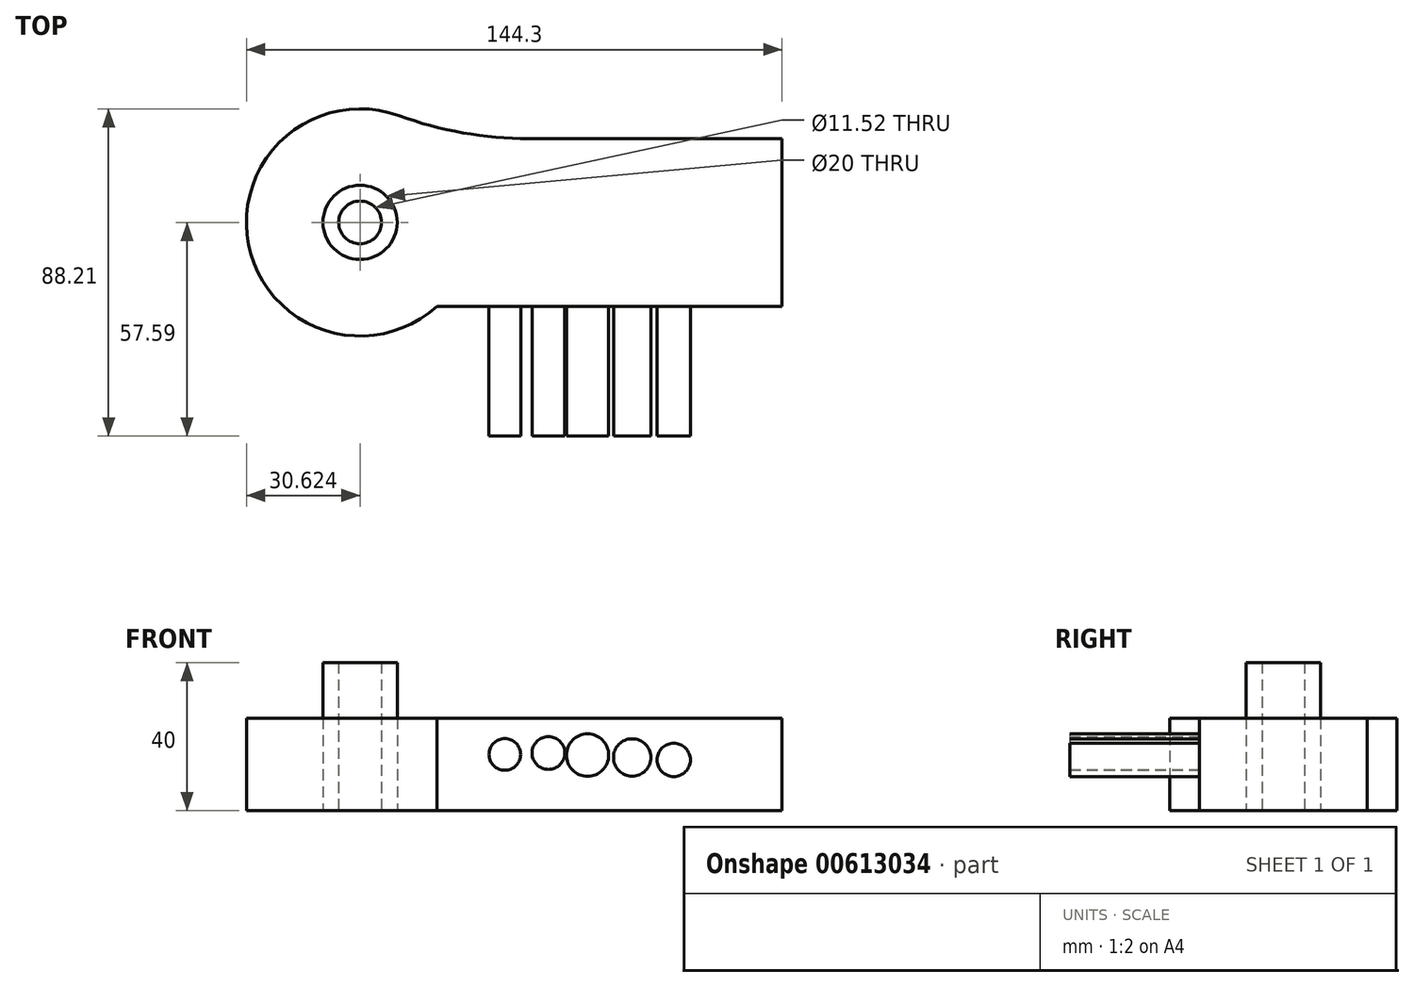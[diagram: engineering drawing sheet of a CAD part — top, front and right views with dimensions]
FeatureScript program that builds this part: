
annotation { "Feature Type Name" : "Feature", "Feature Type Description" : "" }
export const myFeature = defineFeature(function(context is Context, id is Id, definition is map)
    precondition{}
    {
        {
            var Q0;
            Q0=qCreatedBy(makeId("Top.planeOp"),FACE);
            var sketch = newSketch(context, id + "F0", { "sketchPlane" : qUnion([Q0])});
            skLineSegment(sketch, "E0.bottom", {"start": v(-54.54, 21.04) * mm, "end": v(59.14, 21.04) * mm});
            skLineSegment(sketch, "E0.top", {"start": v(-54.54, -24.14) * mm, "end": v(59.14, -24.14) * mm});
            skLineSegment(sketch, "E0.left", {"start": v(-54.54, 21.04) * mm, "end": v(-54.54, -24.14) * mm});
            skLineSegment(sketch, "E0.right", {"start": v(59.14, 21.04) * mm, "end": v(59.14, -24.14) * mm});
            skCircle(sketch, "E1", {"center": v(-54.54, -1.55) * mm, "radius": 30.62 * mm});
            skArc(sketch, "E2", {"start": v(-44.06, 27.22) * mm, "mid": v(-26.82, 22.6) * mm, "end": v(-9.04, 21.04) * mm});
            skCircle(sketch, "E3", {"center": v(-54.54, -1.55) * mm, "radius": 10 * mm});
            skCircle(sketch, "E4", {"center": v(-54.54, -1.55) * mm, "radius": 5.76 * mm});
            skSolve(sketch);
        }
        {
            var Q0;
            Q0 = qSketchRegion(id + "F0", true);
            extrude(context, id + "F1", {"entities" : qUnion([Q0]), "depth" : 25 * mm, "offsetDistance" : 25 * mm});
        }
        {
            var Q0;
            {var subQ0=sQuery(id+"F0.wireOp",EDGE,"E3");var subQ1=sQuery(id+"F0.wireOp",EDGE,"E0.left");var subQ2=makeQuery(id+"F0.imprint","INTERSECT",VERTEX,{"disambiguationData":[OD(0.0)],"derivedFrom":[subQ1,subQ0]});Q0=makeQuery(id+"F0.imprint","IMPRINT",FACE,{"disambiguationData":[TD([[makeQuery(id+"F0.imprint","IMPRINT",EDGE,{"disambiguationData":[TD([[subQ2,-1.0]])],"derivedFrom":subQ1}),1.0]])]});}
            var Q1;
            {var subQ0=sQuery(id+"F0.wireOp",EDGE,"E3");var subQ1=sQuery(id+"F0.wireOp",EDGE,"E0.left");var subQ2=makeQuery(id+"F0.imprint","INTERSECT",VERTEX,{"disambiguationData":[OD(0.0)],"derivedFrom":[subQ1,subQ0]});Q1=makeQuery(id+"F0.imprint","IMPRINT",FACE,{"disambiguationData":[TD([[makeQuery(id+"F0.imprint","IMPRINT",EDGE,{"disambiguationData":[TD([[subQ2,-1.0]])],"derivedFrom":subQ1}),-1.0]])]});}
            extrude(context, id + "F2", {"entities" : qUnion([Q0, Q1]), "depth" : 40 * mm, "offsetDistance" : 25 * mm});
        }
        {
            var Q0;
            Q0=makeQuery(id+"F1.opExtrude","SWEPT_FACE",FACE,{"disambiguationData":[OSD([sQuery(id+"F0.wireOp",EDGE,"E0.top")])]});
            var sketch = newSketch(context, id + "F3", { "sketchPlane" : qUnion([Q0])});
            skCircle(sketch, "E5", {"center": v(-15.53, 15.2) * mm, "radius": 4.26 * mm});
            skCircle(sketch, "E6", {"center": v(-3.77, 15.58) * mm, "radius": 4.42 * mm});
            skCircle(sketch, "E7", {"center": v(6.77, 15.02) * mm, "radius": 5.7 * mm});
            skCircle(sketch, "E8", {"center": v(18.8, 14.37) * mm, "radius": 5.04 * mm});
            skCircle(sketch, "E9", {"center": v(30, 13.72) * mm, "radius": 4.48 * mm});
            skSolve(sketch);
        }
        {
            var Q0;
            Q0=makeQuery(id+"F3.imprint","IMPRINT",FACE,{"disambiguationData":[TD([[makeQuery(id+"F3.imprint","IMPRINT",EDGE,{"derivedFrom":sQuery(id+"F3.wireOp",EDGE,"E5")}),1.0]])]});
            var Q1;
            Q1=makeQuery(id+"F3.imprint","IMPRINT",FACE,{"disambiguationData":[TD([[makeQuery(id+"F3.imprint","IMPRINT",EDGE,{"derivedFrom":sQuery(id+"F3.wireOp",EDGE,"E6")}),1.0]])]});
            var Q2;
            Q2=makeQuery(id+"F3.imprint","IMPRINT",FACE,{"disambiguationData":[TD([[makeQuery(id+"F3.imprint","IMPRINT",EDGE,{"derivedFrom":sQuery(id+"F3.wireOp",EDGE,"E7")}),1.0]])]});
            var Q3;
            Q3=makeQuery(id+"F3.imprint","IMPRINT",FACE,{"disambiguationData":[TD([[makeQuery(id+"F3.imprint","IMPRINT",EDGE,{"derivedFrom":sQuery(id+"F3.wireOp",EDGE,"E8")}),1.0]])]});
            var Q4;
            Q4=makeQuery(id+"F3.imprint","IMPRINT",FACE,{"disambiguationData":[TD([[makeQuery(id+"F3.imprint","IMPRINT",EDGE,{"derivedFrom":sQuery(id+"F3.wireOp",EDGE,"E9")}),1.0]])]});
            var Q5;
            Q5=makeQuery(id+"F3.imprint","IMPRINT",FACE,{"disambiguationData":[TD([[makeQuery(id+"F3.imprint","IMPRINT",EDGE,{"derivedFrom":sQuery(id+"F3.wireOp",EDGE,"E9")}),1.0]])]});
            extrude(context, id + "F4", {"entities" : qUnion([Q0, Q1, Q2, Q3, Q4, Q5]), "operationType" : NewBodyOperationType.ADD, "endBound" : BoundingType.SYMMETRIC, "depth" : 70 * mm, "offsetDistance" : 25 * mm});
        }
    });
